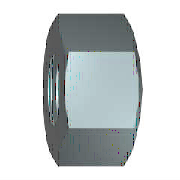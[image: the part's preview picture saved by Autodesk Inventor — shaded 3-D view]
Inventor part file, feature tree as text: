
AUTODESK INVENTOR PART (.ipt)
format: ipt  version: 2017 (Build 210142000, 142)  size: 166,912 bytes
history: native  units: mm (DEFAULTED — no unit token found)
features: sketch x3, other x2, hole x1, chamfer x1, plane x1
ambient origin geometry x7: Origin, YZ Plane, XY Plane, X Axis, Y Axis, Z Axis, Center Point
bodies: Solid1 (feature_tree), Body (feature_tree)
feature tree (8):
  hole  "Thread"  [1 undecoded]
  sketch  "Sketch3"  dims[d3=4.917mm d4=6.0mm d5=4.0mm d6=2.0mm d7=14.3117mm d8=4.180449mm d9=120.0deg d10=0.541266mm d11=30.0deg d12=10.0mm d13=30.0deg d14=12.0mm d15=90.0deg d16=90.0deg d19=0.0mm d20=0.541266mm d21=0.0mm d22=0.0mm]
  chamfer  "Chamfer2"  Angle=120.0deg  [1 undecoded]
  other  "Cut1"
  other  "Work Axis1"
  plane  "Work Plane1"
  sketch  "Sketch1"  dims[d0=10.0mm d1=9.0mm]
  sketch  "Sketch2"  dims[d2=0.0mm]
note: 2 required parameter values undecoded (feature->parameter linkage not recoverable at this tier; creation-order binding heuristic only, values carry confidence <= 0.55)
